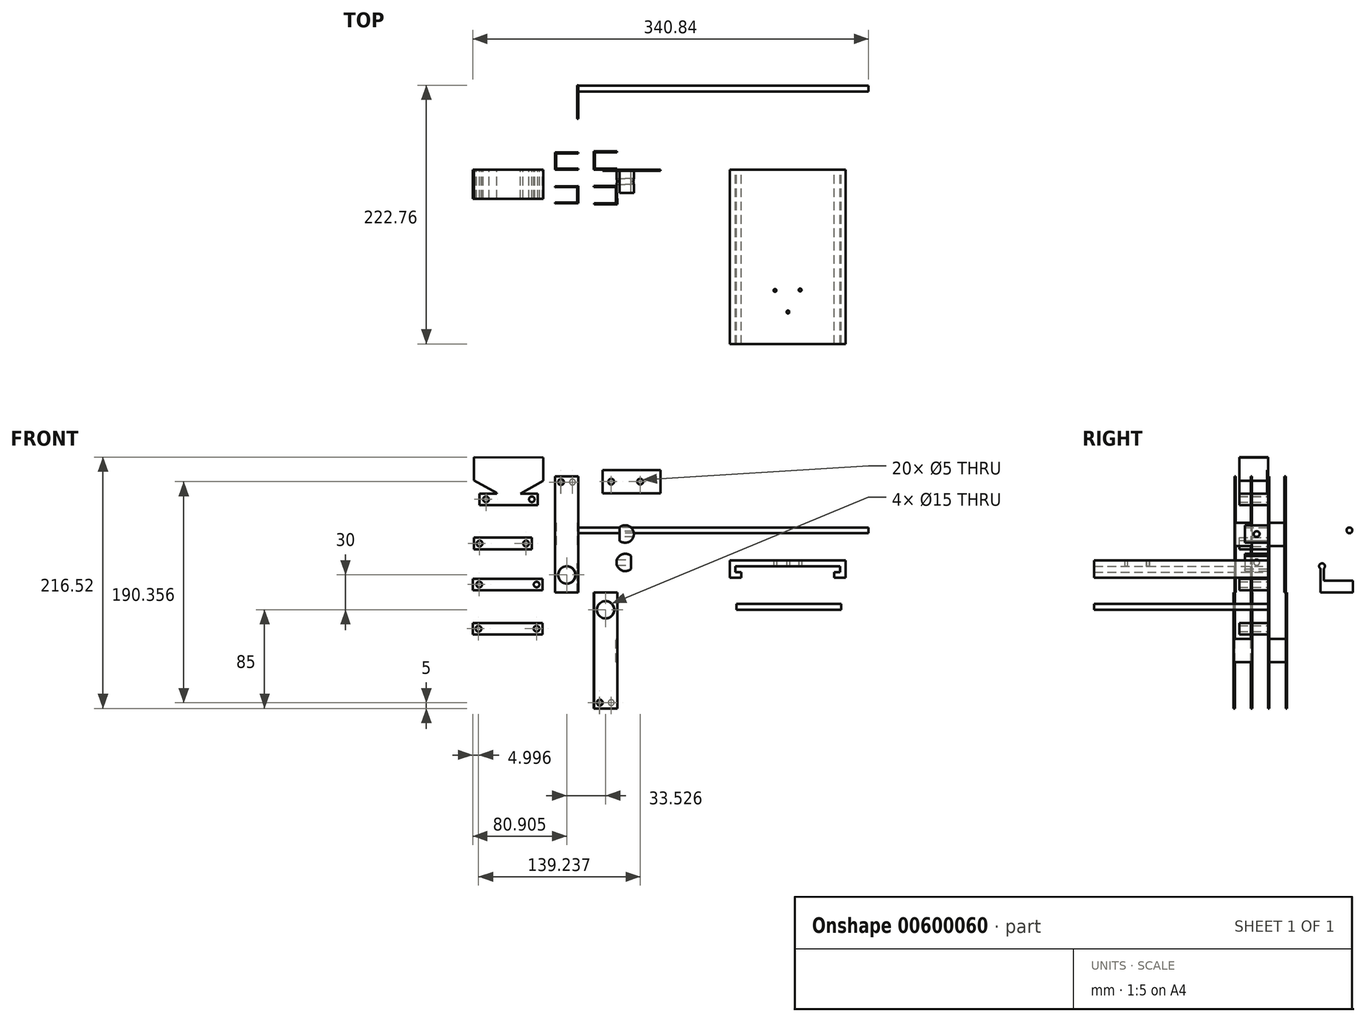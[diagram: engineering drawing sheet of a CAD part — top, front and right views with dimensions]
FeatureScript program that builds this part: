
annotation { "Feature Type Name" : "Feature", "Feature Type Description" : "" }
export const myFeature = defineFeature(function(context is Context, id is Id, definition is map)
    precondition{}
    {
        {
            var Q0;
            Q0=qCreatedBy(makeId("Top.planeOp"),FACE);
            var sketch = newSketch(context, id + "F0", { "sketchPlane" : qUnion([Q0])});
            skLineSegment(sketch, "E0", {"start": v(0, 15) * mm, "end": v(-20, 15) * mm});
            skLineSegment(sketch, "E1", {"start": v(-20, 15) * mm, "end": v(-20, 0) * mm});
            skLineSegment(sketch, "E2", {"start": v(-20, 0) * mm, "end": v(0, 0) * mm});
            skLineSegment(sketch, "E3", {"start": v(0, 0) * mm, "end": v(0, 1) * mm});
            skLineSegment(sketch, "E4", {"start": v(0, 1) * mm, "end": v(-19, 1) * mm});
            skLineSegment(sketch, "E5", {"start": v(-19, 1) * mm, "end": v(-19, 14) * mm});
            skLineSegment(sketch, "E6", {"start": v(-19, 14) * mm, "end": v(0, 14) * mm});
            skLineSegment(sketch, "E7", {"start": v(0, 14) * mm, "end": v(0, 15) * mm});
            skLineSegment(sketch, "E8", {"start": v(33.42, 1) * mm, "end": v(14.42, 1) * mm});
            skLineSegment(sketch, "E9", {"start": v(14.42, 1) * mm, "end": v(14.42, 15) * mm});
            skLineSegment(sketch, "E10", {"start": v(14.42, 15) * mm, "end": v(33.42, 15) * mm});
            skLineSegment(sketch, "E11", {"start": v(33.42, 15) * mm, "end": v(33.42, 16) * mm});
            skLineSegment(sketch, "E12", {"start": v(33.42, 16) * mm, "end": v(13.42, 16) * mm});
            skLineSegment(sketch, "E13", {"start": v(13.42, 16) * mm, "end": v(13.42, 0) * mm});
            skLineSegment(sketch, "E14", {"start": v(13.42, 0) * mm, "end": v(33.42, 0) * mm});
            skLineSegment(sketch, "E15", {"start": v(33.42, 0) * mm, "end": v(33.42, 1) * mm});
            skLineSegment(sketch, "E16", {"start": v(-36.62, -7.13) * mm, "end": v(38.64, -6.85) * mm, "construction": true});
            skLineSegment(sketch, "E17.MirrorCS", {"start": v(-19, 16) * mm, "end": v(0, 16) * mm});
            skLineSegment(sketch, "E18.MirrorCS", {"start": v(-19.95, -14.13) * mm, "end": v(0.05, -13.99) * mm});
            skLineSegment(sketch, "E19.MirrorCS", {"start": v(0.16, -28.99) * mm, "end": v(-19.84, -29.13) * mm});
            skLineSegment(sketch, "E20.MirrorCS", {"start": v(13.47, -13.89) * mm, "end": v(33.47, -13.74) * mm});
            skLineSegment(sketch, "E21.MirrorCS", {"start": v(33.58, -29.74) * mm, "end": v(13.58, -29.89) * mm});
            skLineSegment(sketch, "E22", {"start": v(13.47, -13.89) * mm, "end": v(13.47, -14.89) * mm});
            skLineSegment(sketch, "E23", {"start": v(13.47, -14.89) * mm, "end": v(32.47, -14.75) * mm});
            skLineSegment(sketch, "E24", {"start": v(32.58, -28.75) * mm, "end": v(13.58, -28.89) * mm});
            skLineSegment(sketch, "E25", {"start": v(13.58, -28.89) * mm, "end": v(13.58, -29.89) * mm});
            skLineSegment(sketch, "E26", {"start": v(32.58, -28.75) * mm, "end": v(32.47, -14.75) * mm});
            skLineSegment(sketch, "E27", {"start": v(33.47, -13.74) * mm, "end": v(33.58, -29.74) * mm});
            skLineSegment(sketch, "E28", {"start": v(0.05, -13.99) * mm, "end": v(0.16, -28.99) * mm});
            skLineSegment(sketch, "E29", {"start": v(-19.95, -14.13) * mm, "end": v(-19.94, -15.13) * mm});
            skLineSegment(sketch, "E30", {"start": v(-19.94, -15.13) * mm, "end": v(-0.94, -15) * mm});
            skLineSegment(sketch, "E31", {"start": v(-0.94, -15) * mm, "end": v(-0.85, -28) * mm});
            skLineSegment(sketch, "E32", {"start": v(-0.85, -28) * mm, "end": v(-19.84, -28.13) * mm});
            skLineSegment(sketch, "E33", {"start": v(-19.84, -29.13) * mm, "end": v(-19.84, -28.13) * mm});
            skSolve(sketch);
        }
        {
            var Q0;
            Q0=makeQuery(id+"F0.imprint","IMPRINT",FACE,{"disambiguationData":[TD([[makeQuery(id+"F0.imprint","IMPRINT",EDGE,{"derivedFrom":sQuery(id+"F0.wireOp",EDGE,"E0")}),1.0]])]});
            var Q1;
            Q1=makeQuery(id+"F0.imprint","IMPRINT",FACE,{"disambiguationData":[TD([[makeQuery(id+"F0.imprint","IMPRINT",EDGE,{"derivedFrom":sQuery(id+"F0.wireOp",EDGE,"E19.MirrorCS")}),-1.0]])]});
            extrude(context, id + "F1", {"entities" : qUnion([Q0, Q1]), "depth" : 100 * mm, "offsetDistance" : 25 * mm});
        }
        {
            var Q0;
            Q0=makeQuery(id+"F1.opExtrude","SWEPT_FACE",FACE,{"disambiguationData":[OSD([sQuery(id+"F0.wireOp",EDGE,"E2")])]});
            var sketch = newSketch(context, id + "F2", { "sketchPlane" : qUnion([Q0])});
            skCircle(sketch, "E34", {"center": v(-10, 15) * mm, "radius": 7.5 * mm});
            skPoint(sketch, "E34.centerSnap0", {"position": v(-10, 0) * mm});
            skCircle(sketch, "E35", {"center": v(-5, 95) * mm, "radius": 2.5 * mm});
            skSolve(sketch);
        }
        {
            var Q0;
            Q0=makeQuery(id+"F2.imprint","IMPRINT",FACE,{"disambiguationData":[TD([[makeQuery(id+"F2.imprint","IMPRINT",EDGE,{"derivedFrom":sQuery(id+"F2.wireOp",EDGE,"E34")}),1.0]])]});
            var Q1;
            Q1=makeQuery(id+"F2.imprint","IMPRINT",FACE,{"disambiguationData":[TD([[makeQuery(id+"F2.imprint","IMPRINT",EDGE,{"derivedFrom":sQuery(id+"F2.wireOp",EDGE,"E35")}),1.0]])]});
            extrude(context, id + "F3", {"entities" : qUnion([Q0, Q1]), "operationType" : NewBodyOperationType.REMOVE, "endBound" : BoundingType.THROUGH_ALL, "oppositeDirection" : true, "depth" : 25 * mm, "offsetDistance" : 25 * mm});
        }
        {
            var Q0;
            Q0=makeQuery(id+"F1.opExtrude","SWEPT_FACE",FACE,{"disambiguationData":[OSD([sQuery(id+"F0.wireOp",EDGE,"E1")])]});
            var sketch = newSketch(context, id + "F4", { "sketchPlane" : qUnion([Q0])});
            skPoint(sketch, "E36.centerSnap0", {"position": v(-7.5, 0) * mm});
            skLineSegment(sketch, "E37", {"start": v(-14, 0) * mm, "end": v(-14, 40) * mm});
            skLineSegment(sketch, "E38", {"start": v(-14, 40) * mm, "end": v(-1, 40) * mm});
            skLineSegment(sketch, "E39", {"start": v(-1, 40) * mm, "end": v(-1, 0) * mm});
            skLineSegment(sketch, "E40", {"start": v(-14, 100) * mm, "end": v(-14, 60) * mm});
            skLineSegment(sketch, "E41", {"start": v(-14, 60) * mm, "end": v(-1, 60) * mm});
            skLineSegment(sketch, "E42", {"start": v(-1, 60) * mm, "end": v(-1, 100) * mm});
            skSolve(sketch);
        }
        {
            var Q0;
            {var subQ0=sQuery(id+"F4.wireOp",EDGE,"E37");Q0=makeQuery(id+"F4.imprint","IMPRINT",FACE,{"disambiguationData":[TD([[makeQuery(id+"F4.imprint","IMPRINT",EDGE,{"derivedFrom":subQ0}),-1.0]])]});}
            var Q1;
            {var subQ0=sQuery(id+"F4.wireOp",EDGE,"E40");Q1=makeQuery(id+"F4.imprint","IMPRINT",FACE,{"disambiguationData":[TD([[makeQuery(id+"F4.imprint","IMPRINT",EDGE,{"derivedFrom":subQ0}),1.0]])]});}
            extrude(context, id + "F5", {"entities" : qUnion([Q0, Q1]), "operationType" : NewBodyOperationType.REMOVE, "endBound" : BoundingType.THROUGH_ALL, "oppositeDirection" : true, "depth" : 25 * mm, "offsetDistance" : 25 * mm});
        }
        {
            var Q0;
            Q0=makeQuery(id+"F0.imprint","IMPRINT",FACE,{"disambiguationData":[TD([[makeQuery(id+"F0.imprint","IMPRINT",EDGE,{"derivedFrom":sQuery(id+"F0.wireOp",EDGE,"E8")}),1.0]])]});
            var Q1;
            Q1=makeQuery(id+"F0.imprint","IMPRINT",FACE,{"disambiguationData":[TD([[makeQuery(id+"F0.imprint","IMPRINT",EDGE,{"derivedFrom":sQuery(id+"F0.wireOp",EDGE,"E20.MirrorCS")}),-1.0]])]});
            extrude(context, id + "F6", {"entities" : qUnion([Q0, Q1]), "oppositeDirection" : true, "depth" : 100 * mm, "offsetDistance" : 25 * mm});
        }
        {
            var Q0;
            Q0=makeQuery(id+"F6.opExtrude","SWEPT_FACE",FACE,{"disambiguationData":[OSD([sQuery(id+"F0.wireOp",EDGE,"E14")])]});
            var sketch = newSketch(context, id + "F7", { "sketchPlane" : qUnion([Q0])});
            skCircle(sketch, "E43", {"center": v(23.42, -15) * mm, "radius": 7.5 * mm});
            skPoint(sketch, "E43.centerSnap0", {"position": v(23.42, 0) * mm});
            skCircle(sketch, "E44", {"center": v(28.42, -95) * mm, "radius": 2.5 * mm});
            skSolve(sketch);
        }
        {
            var Q0;
            Q0=makeQuery(id+"F7.imprint","IMPRINT",FACE,{"disambiguationData":[TD([[makeQuery(id+"F7.imprint","IMPRINT",EDGE,{"derivedFrom":sQuery(id+"F7.wireOp",EDGE,"E43")}),1.0]])]});
            var Q1;
            Q1=makeQuery(id+"F7.imprint","IMPRINT",FACE,{"disambiguationData":[TD([[makeQuery(id+"F7.imprint","IMPRINT",EDGE,{"derivedFrom":sQuery(id+"F7.wireOp",EDGE,"E44")}),1.0]])]});
            extrude(context, id + "F8", {"entities" : qUnion([Q0, Q1]), "operationType" : NewBodyOperationType.REMOVE, "endBound" : BoundingType.THROUGH_ALL, "oppositeDirection" : true, "depth" : 25 * mm, "offsetDistance" : 25 * mm});
        }
        {
            var Q0;
            Q0=makeQuery(id+"F6.opExtrude","SWEPT_FACE",FACE,{"disambiguationData":[OSD([sQuery(id+"F0.wireOp",EDGE,"E13")])]});
            var sketch = newSketch(context, id + "F9", { "sketchPlane" : qUnion([Q0])});
            skLineSegment(sketch, "E45", {"start": v(-15, 0) * mm, "end": v(-15, -40) * mm});
            skLineSegment(sketch, "E46", {"start": v(-15, -40) * mm, "end": v(-1, -40) * mm});
            skLineSegment(sketch, "E47", {"start": v(-1, -40) * mm, "end": v(-1, 0) * mm});
            skLineSegment(sketch, "E48", {"start": v(-15, -100) * mm, "end": v(-15, -60) * mm});
            skLineSegment(sketch, "E49", {"start": v(-15, -60) * mm, "end": v(-1, -60) * mm});
            skLineSegment(sketch, "E50", {"start": v(-1, -60) * mm, "end": v(-1, -100) * mm});
            skSolve(sketch);
        }
        {
            var Q0;
            {var subQ0=sQuery(id+"F9.wireOp",EDGE,"E45");Q0=makeQuery(id+"F9.imprint","IMPRINT",FACE,{"disambiguationData":[TD([[makeQuery(id+"F9.imprint","IMPRINT",EDGE,{"derivedFrom":subQ0}),1.0]])]});}
            var Q1;
            {var subQ0=sQuery(id+"F9.wireOp",EDGE,"E48");Q1=makeQuery(id+"F9.imprint","IMPRINT",FACE,{"disambiguationData":[TD([[makeQuery(id+"F9.imprint","IMPRINT",EDGE,{"derivedFrom":subQ0}),-1.0]])]});}
            extrude(context, id + "F10", {"entities" : qUnion([Q0, Q1]), "operationType" : NewBodyOperationType.REMOVE, "endBound" : BoundingType.THROUGH_ALL, "oppositeDirection" : true, "depth" : 25 * mm, "offsetDistance" : 25 * mm});
        }
        {
            var Q0;
            Q0=qCreatedBy(makeId("Front.planeOp"),FACE);
            var sketch = newSketch(context, id + "F11", { "sketchPlane" : qUnion([Q0])});
            skLineSegment(sketch, "E51.bottom", {"start": v(20.9, 105.36) * mm, "end": v(70.9, 105.36) * mm});
            skLineSegment(sketch, "E51.top", {"start": v(20.9, 85.36) * mm, "end": v(70.9, 85.36) * mm});
            skLineSegment(sketch, "E51.left", {"start": v(20.9, 105.36) * mm, "end": v(20.9, 85.36) * mm});
            skLineSegment(sketch, "E51.right", {"start": v(70.9, 105.36) * mm, "end": v(70.9, 85.36) * mm});
            skCircle(sketch, "E52", {"center": v(28.4, 95.36) * mm, "radius": 2.5 * mm});
            skPoint(sketch, "E52.centerSnap0", {"position": v(20.9, 95.36) * mm});
            skCircle(sketch, "E53.MirrorC", {"center": v(53.4, 95.36) * mm, "radius": 2.5 * mm});
            skSolve(sketch);
        }
        {
            var Q0;
            Q0=makeQuery(id+"F11.imprint","IMPRINT",FACE,{"disambiguationData":[TD([[makeQuery(id+"F11.imprint","IMPRINT",EDGE,{"derivedFrom":sQuery(id+"F11.wireOp",EDGE,"E51.bottom")}),-1.0]])]});
            extrude(context, id + "F12", {"entities" : qUnion([Q0]), "depth" : 1 * mm, "offsetDistance" : 25 * mm});
        }
        {
            var Q0;
            Q0=makeQuery(id+"F1.opExtrude","SWEPT_FACE",FACE,{"disambiguationData":[OSD([sQuery(id+"F0.wireOp",EDGE,"E19.MirrorCS")])]});
            var sketch = newSketch(context, id + "F13", { "sketchPlane" : qUnion([Q0])});
            skCircle(sketch, "E54", {"center": v(-15.05, 95) * mm, "radius": 2.5 * mm});
            skCircle(sketch, "E55", {"center": v(-10.05, 15) * mm, "radius": 7.5 * mm});
            skPoint(sketch, "E55.centerSnap0", {"position": v(-10.05, 0) * mm});
            skSolve(sketch);
        }
        {
            var Q0;
            Q0=makeQuery(id+"F13.imprint","IMPRINT",FACE,{"disambiguationData":[TD([[makeQuery(id+"F13.imprint","IMPRINT",EDGE,{"derivedFrom":sQuery(id+"F13.wireOp",EDGE,"E54")}),1.0]])]});
            var Q1;
            Q1=makeQuery(id+"F13.imprint","IMPRINT",FACE,{"disambiguationData":[TD([[makeQuery(id+"F13.imprint","IMPRINT",EDGE,{"derivedFrom":sQuery(id+"F13.wireOp",EDGE,"E55")}),1.0]])]});
            extrude(context, id + "F14", {"entities" : qUnion([Q0, Q1]), "operationType" : NewBodyOperationType.REMOVE, "endBound" : BoundingType.THROUGH_ALL, "oppositeDirection" : true, "depth" : 25 * mm, "offsetDistance" : 25 * mm});
        }
        {
            var Q0;
            Q0=makeQuery(id+"F6.opExtrude","SWEPT_FACE",FACE,{"disambiguationData":[OSD([sQuery(id+"F0.wireOp",EDGE,"E21.MirrorCS")])]});
            var sketch = newSketch(context, id + "F15", { "sketchPlane" : qUnion([Q0])});
            skCircle(sketch, "E56", {"center": v(23.36, -15) * mm, "radius": 7.5 * mm});
            skPoint(sketch, "E56.centerSnap0", {"position": v(23.36, 0) * mm});
            skCircle(sketch, "E57", {"center": v(18.36, -95) * mm, "radius": 2.5 * mm});
            skSolve(sketch);
        }
        {
            var Q0;
            Q0=qSketchRegion(id+"F15",true);
            extrude(context, id + "F16", {"entities" : qUnion([Q0]), "operationType" : NewBodyOperationType.REMOVE, "endBound" : BoundingType.THROUGH_ALL, "oppositeDirection" : true, "depth" : 25 * mm, "offsetDistance" : 25 * mm});
        }
        {
            var Q0;
            Q0=makeQuery(id+"F6.opExtrude","SWEPT_FACE",FACE,{"disambiguationData":[OSD([sQuery(id+"F0.wireOp",EDGE,"E27")])]});
            var sketch = newSketch(context, id + "F17", { "sketchPlane" : qUnion([Q0])});
            skLineSegment(sketch, "E58", {"start": v(-14.99, -40) * mm, "end": v(-28.99, -40) * mm});
            skLineSegment(sketch, "E59", {"start": v(-28.99, -40) * mm, "end": v(-28.99, 0) * mm});
            skLineSegment(sketch, "E60", {"start": v(-14.99, -40) * mm, "end": v(-14.99, 0) * mm});
            skLineSegment(sketch, "E61", {"start": v(-28.99, -100) * mm, "end": v(-28.99, -60) * mm});
            skLineSegment(sketch, "E62", {"start": v(-28.99, -60) * mm, "end": v(-14.99, -60) * mm});
            skLineSegment(sketch, "E63", {"start": v(-14.99, -60) * mm, "end": v(-14.99, -100) * mm});
            skSolve(sketch);
        }
        {
            var Q0;
            Q0=makeQuery(id+"F17.imprint","IMPRINT",FACE,{"disambiguationData":[TD([[makeQuery(id+"F17.imprint","IMPRINT",EDGE,{"derivedFrom":sQuery(id+"F17.wireOp",EDGE,"E58")}),-1.0]])]});
            var Q1;
            {var subQ0=sQuery(id+"F17.wireOp",EDGE,"E61");Q1=makeQuery(id+"F17.imprint","IMPRINT",FACE,{"disambiguationData":[TD([[makeQuery(id+"F17.imprint","IMPRINT",EDGE,{"derivedFrom":subQ0}),-1.0]])]});}
            extrude(context, id + "F18", {"entities" : qUnion([Q0, Q1]), "operationType" : NewBodyOperationType.REMOVE, "endBound" : BoundingType.THROUGH_ALL, "oppositeDirection" : true, "depth" : 25 * mm, "offsetDistance" : 25 * mm});
        }
        {
            var Q0;
            Q0=makeQuery(id+"F1.opExtrude","SWEPT_FACE",FACE,{"disambiguationData":[OSD([sQuery(id+"F0.wireOp",EDGE,"E28")])]});
            var sketch = newSketch(context, id + "F19", { "sketchPlane" : qUnion([Q0])});
            skLineSegment(sketch, "E64", {"start": v(-14.99, 0) * mm, "end": v(-14.99, 40) * mm});
            skLineSegment(sketch, "E65", {"start": v(-14.99, 40) * mm, "end": v(-27.99, 40) * mm});
            skLineSegment(sketch, "E66", {"start": v(-27.99, 40) * mm, "end": v(-27.99, 0) * mm});
            skLineSegment(sketch, "E67", {"start": v(-27.99, 100) * mm, "end": v(-27.99, 60) * mm});
            skLineSegment(sketch, "E68", {"start": v(-27.99, 60) * mm, "end": v(-14.99, 60) * mm});
            skLineSegment(sketch, "E69", {"start": v(-14.99, 60) * mm, "end": v(-14.99, 100) * mm});
            skSolve(sketch);
        }
        {
            var Q0;
            {var subQ0=sQuery(id+"F19.wireOp",EDGE,"E64");Q0=makeQuery(id+"F19.imprint","IMPRINT",FACE,{"disambiguationData":[TD([[makeQuery(id+"F19.imprint","IMPRINT",EDGE,{"derivedFrom":subQ0}),1.0]])]});}
            var Q1;
            {var subQ0=sQuery(id+"F19.wireOp",EDGE,"E67");Q1=makeQuery(id+"F19.imprint","IMPRINT",FACE,{"disambiguationData":[TD([[makeQuery(id+"F19.imprint","IMPRINT",EDGE,{"derivedFrom":subQ0}),1.0]])]});}
            extrude(context, id + "F20", {"entities" : qUnion([Q0, Q1]), "operationType" : NewBodyOperationType.REMOVE, "oppositeDirection" : true, "depth" : 25 * mm, "offsetDistance" : 25 * mm});
        }
        {
            var Q0;
            Q0=qCreatedBy(makeId("Front.planeOp"),FACE);
            var sketch = newSketch(context, id + "F21", { "sketchPlane" : qUnion([Q0])});
            skArc(sketch, "E70", {"start": v(35.49, 44.6) * mm, "mid": v(47.93, 50.24) * mm, "end": v(35.49, 55.88) * mm});
            skArc(sketch, "E71", {"start": v(45.38, 31.4) * mm, "mid": v(32.93, 25.77) * mm, "end": v(45.38, 20.13) * mm});
            skLineSegment(sketch, "E72", {"start": v(35.49, 55.88) * mm, "end": v(35.49, 44.6) * mm});
            skLineSegment(sketch, "E73.trimOffspring", {"start": v(45.38, 31.4) * mm, "end": v(45.38, 20.13) * mm});
            skPoint(sketch, "E74.orphan", {"position": v(40.43, 57.74) * mm});
            skSolve(sketch);
        }
        {
            var Q0;
            Q0=makeQuery(id+"F21.imprint","IMPRINT",FACE,{"disambiguationData":[TD([[makeQuery(id+"F21.imprint","IMPRINT",EDGE,{"derivedFrom":sQuery(id+"F21.wireOp",EDGE,"E70")}),1.0]])]});
            var Q1;
            Q1=makeQuery(id+"F21.imprint","IMPRINT",FACE,{"disambiguationData":[TD([[makeQuery(id+"F21.imprint","IMPRINT",EDGE,{"derivedFrom":sQuery(id+"F21.wireOp",EDGE,"E71")}),1.0]])]});
            extrude(context, id + "F22", {"entities" : qUnion([Q0, Q1]), "depth" : 20 * mm, "offsetDistance" : 25 * mm});
        }
        {
            var Q0;
            Q0=qCreatedBy(makeId("Right.planeOp"),FACE);
            var sketch = newSketch(context, id + "F23", { "sketchPlane" : qUnion([Q0])});
            skCircle(sketch, "E75", {"center": v(69.88, 53.43) * mm, "radius": 2.5 * mm});
            skSolve(sketch);
        }
        {
            var Q0;
            Q0=makeQuery(id+"F23.imprint","IMPRINT",FACE,{"disambiguationData":[TD([[makeQuery(id+"F23.imprint","IMPRINT",EDGE,{"derivedFrom":sQuery(id+"F23.wireOp",EDGE,"E75")}),1.0]])]});
            extrude(context, id + "F24", {"entities" : qUnion([Q0]), "depth" : 250 * mm, "offsetDistance" : 25 * mm});
        }
        {
            var Q0;
            Q0=qCreatedBy(makeId("Front.planeOp"),FACE);
            var sketch = newSketch(context, id + "F25", { "sketchPlane" : qUnion([Q0])});
            skLineSegment(sketch, "E76.top", {"start": v(-84.95, 75.12) * mm, "end": v(-34.95, 75.12) * mm});
            skLineSegment(sketch, "E76.left", {"start": v(-84.95, 85.12) * mm, "end": v(-84.95, 75.12) * mm});
            skLineSegment(sketch, "E76.right", {"start": v(-34.95, 85.12) * mm, "end": v(-34.95, 75.12) * mm});
            skCircle(sketch, "E77", {"center": v(-79.38, 80.12) * mm, "radius": 2.5 * mm});
            skPoint(sketch, "E77.centerSnap0", {"position": v(-84.95, 80.12) * mm});
            skCircle(sketch, "E78", {"center": v(-39.95, 80.12) * mm, "radius": 2.41 * mm});
            skPoint(sketch, "E78.centerSnap0", {"position": v(-34.95, 80.12) * mm});
            skLineSegment(sketch, "E79.MirrorCS", {"start": v(-89.95, 47.06) * mm, "end": v(-39.95, 47.06) * mm});
            skLineSegment(sketch, "E80.MirrorCS", {"start": v(-89.95, 37.06) * mm, "end": v(-89.95, 47.06) * mm});
            skLineSegment(sketch, "E81.MirrorCS", {"start": v(-89.95, 37.06) * mm, "end": v(-39.95, 37.06) * mm});
            skLineSegment(sketch, "E82.MirrorCS", {"start": v(-39.95, 37.06) * mm, "end": v(-39.95, 47.06) * mm});
            skCircle(sketch, "E83", {"center": v(-84.95, 42.06) * mm, "radius": 2.5 * mm});
            skPoint(sketch, "E83.centerSnap0", {"position": v(-89.95, 42.06) * mm});
            skCircle(sketch, "E84", {"center": v(-44.95, 42.06) * mm, "radius": 2.5 * mm});
            skPoint(sketch, "E84.centerSnap0", {"position": v(-39.95, 42.06) * mm});
            skLineSegment(sketch, "E85.bottom", {"start": v(-90.84, 11.74) * mm, "end": v(-30.84, 11.74) * mm});
            skLineSegment(sketch, "E85.top", {"start": v(-90.84, 1.74) * mm, "end": v(-30.84, 1.74) * mm});
            skLineSegment(sketch, "E85.left", {"start": v(-90.84, 11.74) * mm, "end": v(-90.84, 1.74) * mm});
            skLineSegment(sketch, "E85.right", {"start": v(-30.84, 11.74) * mm, "end": v(-30.84, 1.74) * mm});
            skCircle(sketch, "E86", {"center": v(-85.27, 6.74) * mm, "radius": 2.5 * mm});
            skPoint(sketch, "E86.centerSnap0", {"position": v(-90.84, 6.74) * mm});
            skCircle(sketch, "E87", {"center": v(-35.84, 6.74) * mm, "radius": 2.41 * mm});
            skPoint(sketch, "E87.centerSnap0", {"position": v(-30.84, 6.74) * mm});
            skLineSegment(sketch, "E88.MirrorCS", {"start": v(-90.84, -36.32) * mm, "end": v(-90.84, -26.32) * mm});
            skLineSegment(sketch, "E89.MirrorCS", {"start": v(-30.84, -36.32) * mm, "end": v(-30.84, -26.32) * mm});
            skCircle(sketch, "E90", {"center": v(-85.84, -31.32) * mm, "radius": 2.5 * mm});
            skPoint(sketch, "E90.centerSnap0", {"position": v(-90.84, -31.32) * mm});
            skCircle(sketch, "E91", {"center": v(-35.84, -31.32) * mm, "radius": 2.5 * mm});
            skPoint(sketch, "E91.centerSnap0", {"position": v(-30.84, -31.32) * mm});
            skLineSegment(sketch, "E92", {"start": v(-90.84, -26.32) * mm, "end": v(-30.84, -26.32) * mm});
            skLineSegment(sketch, "E93", {"start": v(-90.84, -36.32) * mm, "end": v(-30.84, -36.32) * mm});
            skLineSegment(sketch, "E94", {"start": v(-69.95, 85.12) * mm, "end": v(-69.95, 85.56) * mm});
            skLineSegment(sketch, "E95.MirrorCS", {"start": v(-49.95, 85.12) * mm, "end": v(-49.95, 85.12) * mm});
            skLineSegment(sketch, "E96.MirrorCS", {"start": v(-89.95, 135.12) * mm, "end": v(-39.95, 135.12) * mm});
            skLineSegment(sketch, "E97.MirrorCS", {"start": v(-84.95, 85.12) * mm, "end": v(-69.95, 85.12) * mm});
            skLineSegment(sketch, "E98", {"start": v(-89.95, 96.52) * mm, "end": v(-89.95, 116.52) * mm});
            skLineSegment(sketch, "E99", {"start": v(-29.95, 116.08) * mm, "end": v(-29.95, 96.08) * mm});
            skLineSegment(sketch, "E100.trimOffspring", {"start": v(-49.95, 85.12) * mm, "end": v(-29.95, 96.08) * mm});
            skLineSegment(sketch, "E101", {"start": v(-69.95, 85.56) * mm, "end": v(-89.95, 96.52) * mm});
            skLineSegment(sketch, "E102.trimOffspring", {"start": v(-49.95, 85.12) * mm, "end": v(-34.95, 85.12) * mm});
            skPoint(sketch, "E103.end.orphan", {"position": v(-59.95, 75.12) * mm});
            skPoint(sketch, "E103.start.orphan", {"position": v(-59.95, 85.12) * mm});
            skLineSegment(sketch, "E104", {"start": v(-29.95, 116.08) * mm, "end": v(-89.95, 116.52) * mm});
            skLineSegment(sketch, "E105", {"start": v(-59.95, 75.12) * mm, "end": v(-59.95, 116.3) * mm, "construction": true});
            skSolve(sketch);
        }
        {
            var Q0;
            Q0=makeQuery(id+"F25.imprint","IMPRINT",FACE,{"disambiguationData":[TD([[makeQuery(id+"F25.imprint","IMPRINT",EDGE,{"derivedFrom":sQuery(id+"F25.wireOp",EDGE,"E76.bottom")}),-1.0]])]});
            var Q1;
            {var subQ2=sQuery(id+"F25.wireOp",EDGE,"E80.MirrorCS");Q1=makeQuery(id+"F25.imprint","IMPRINT",FACE,{"disambiguationData":[TD([[makeQuery(id+"F25.imprint","IMPRINT",EDGE,{"derivedFrom":subQ2}),-1.0]])]});}
            var Q2;
            Q2=makeQuery(id+"F25.imprint","IMPRINT",FACE,{"disambiguationData":[TD([[makeQuery(id+"F25.imprint","IMPRINT",EDGE,{"derivedFrom":sQuery(id+"F25.wireOp",EDGE,"E76.top")}),1.0]])]});
            extrude(context, id + "F26", {"entities" : qUnion([Q0, Q1, Q2]), "depth" : 25 * mm, "offsetDistance" : 25 * mm});
        }
        {
            var Q0;
            Q0=makeQuery(id+"F25.imprint","IMPRINT",FACE,{"disambiguationData":[TD([[makeQuery(id+"F25.imprint","IMPRINT",EDGE,{"derivedFrom":sQuery(id+"F25.wireOp",EDGE,"E88.MirrorCS")}),-1.0]])]});
            var Q1;
            Q1=makeQuery(id+"F25.imprint","IMPRINT",FACE,{"disambiguationData":[TD([[makeQuery(id+"F25.imprint","IMPRINT",EDGE,{"derivedFrom":sQuery(id+"F25.wireOp",EDGE,"E85.bottom")}),-1.0]])]});
            extrude(context, id + "F27", {"entities" : qUnion([Q0, Q1]), "depth" : 25 * mm, "offsetDistance" : 25 * mm});
        }
        {
            var Q0;
            Q0=makeQuery(id+"F22.opExtrude","SWEPT_FACE",FACE,{"disambiguationData":[OSD([sQuery(id+"F21.wireOp",EDGE,"E73.trimOffspring")])]});
            var sketch = newSketch(context, id + "F28", { "sketchPlane" : qUnion([Q0])});
            skCircle(sketch, "E106", {"center": v(-10, 25.77) * mm, "radius": 2.5 * mm});
            skPoint(sketch, "E106.centerSnap0", {"position": v(-20, 25.77) * mm});
            skPoint(sketch, "E106.centerSnap1", {"position": v(-10, 31.4) * mm});
            skSolve(sketch);
        }
        {
            var Q0;
            Q0=makeQuery(id+"F28.imprint","IMPRINT",FACE,{"disambiguationData":[TD([[makeQuery(id+"F28.imprint","IMPRINT",EDGE,{"derivedFrom":sQuery(id+"F28.wireOp",EDGE,"E106")}),1.0]])]});
            extrude(context, id + "F29", {"entities" : qUnion([Q0]), "operationType" : NewBodyOperationType.REMOVE, "endBound" : BoundingType.THROUGH_ALL, "oppositeDirection" : true, "depth" : 25 * mm, "offsetDistance" : 25 * mm});
        }
        {
            var Q0;
            Q0=makeQuery(id+"F22.opExtrude","SWEPT_FACE",FACE,{"disambiguationData":[OSD([sQuery(id+"F21.wireOp",EDGE,"E72")])]});
            var sketch = newSketch(context, id + "F30", { "sketchPlane" : qUnion([Q0])});
            skCircle(sketch, "E107", {"center": v(10, 50.24) * mm, "radius": 2.5 * mm});
            skPoint(sketch, "E107.centerSnap0", {"position": v(10, 44.6) * mm});
            skPoint(sketch, "E107.centerSnap1", {"position": v(0, 50.24) * mm});
            skSolve(sketch);
        }
        {
            var Q0;
            Q0=makeQuery(id+"F30.imprint","IMPRINT",FACE,{"disambiguationData":[TD([[makeQuery(id+"F30.imprint","IMPRINT",EDGE,{"derivedFrom":sQuery(id+"F30.wireOp",EDGE,"E107")}),1.0]])]});
            extrude(context, id + "F31", {"entities" : qUnion([Q0]), "operationType" : NewBodyOperationType.REMOVE, "endBound" : BoundingType.THROUGH_ALL, "oppositeDirection" : true, "depth" : 25 * mm, "offsetDistance" : 25 * mm});
        }
        {
            var Q0;
            Q0=qCreatedBy(makeId("Right.planeOp"),FACE);
            var sketch = newSketch(context, id + "F32", { "sketchPlane" : qUnion([Q0])});
            skArc(sketch, "E108", {"start": v(47.76, 20.47) * mm, "mid": v(46.3, 25) * mm, "end": v(44.85, 20.47) * mm});
            skLineSegment(sketch, "E109", {"start": v(47.76, 8.68) * mm, "end": v(47.76, 20.47) * mm});
            skLineSegment(sketch, "E110.MirrorCS", {"start": v(44.85, 8.68) * mm, "end": v(44.85, 20.47) * mm});
            skLineSegment(sketch, "E111", {"start": v(37.92, 27.31) * mm, "end": v(57.96, 27.31) * mm, "construction": true});
            skLineSegment(sketch, "E112", {"start": v(44.85, 8.68) * mm, "end": v(44.85, 0) * mm});
            skLineSegment(sketch, "E113", {"start": v(44.85, 0) * mm, "end": v(47.76, 0) * mm});
            skLineSegment(sketch, "E114", {"start": v(47.76, 0) * mm, "end": v(47.76, 8.68) * mm});
            skArc(sketch, "E115.MirrorCS", {"start": v(47.76, 34.16) * mm, "mid": v(46.3, 29.63) * mm, "end": v(44.85, 34.16) * mm});
            skLineSegment(sketch, "E116.MirrorCS", {"start": v(44.85, 45.94) * mm, "end": v(44.85, 34.16) * mm});
            skLineSegment(sketch, "E117.MirrorCS", {"start": v(47.76, 45.94) * mm, "end": v(47.76, 34.16) * mm});
            skLineSegment(sketch, "E118.MirrorCS", {"start": v(44.85, 45.94) * mm, "end": v(44.85, 54.62) * mm});
            skLineSegment(sketch, "E119.MirrorCS", {"start": v(47.76, 54.62) * mm, "end": v(47.76, 45.94) * mm});
            skLineSegment(sketch, "E120.MirrorCS", {"start": v(44.85, 54.62) * mm, "end": v(47.76, 54.62) * mm});
            skSolve(sketch);
        }
        {
            var Q0;
            Q0=makeQuery(id+"F32.imprint","IMPRINT",FACE,{"disambiguationData":[TD([[makeQuery(id+"F32.imprint","IMPRINT",EDGE,{"derivedFrom":sQuery(id+"F32.wireOp",EDGE,"E108")}),1.0]])]});
            var Q1;
            Q1=makeQuery(id+"F32.imprint","IMPRINT",FACE,{"disambiguationData":[TD([[makeQuery(id+"F32.imprint","IMPRINT",EDGE,{"derivedFrom":sQuery(id+"F32.wireOp",EDGE,"E115.MirrorCS")}),-1.0]])]});
            extrude(context, id + "F33", {"entities" : qUnion([Q0, Q1]), "oppositeDirection" : true, "depth" : 1 * mm, "offsetDistance" : 25 * mm});
        }
        {
            var Q0;
            Q0=makeQuery(id+"F33.opExtrude","SWEPT_FACE",FACE,{"disambiguationData":[OSD([sQuery(id+"F32.wireOp",EDGE,"E109"),sQuery(id+"F32.wireOp",EDGE,"E114")])]});
            var sketch = newSketch(context, id + "F34", { "sketchPlane" : qUnion([Q0])});
            skLineSegment(sketch, "E121", {"start": v(0, 10) * mm, "end": v(1, 10) * mm});
            skLineSegment(sketch, "E122", {"start": v(0.98, 44.62) * mm, "end": v(0, 44.62) * mm});
            skSolve(sketch);
        }
        {
            var Q0;
            {var subQ0=sQuery(id+"F34.wireOp",EDGE,"E121");Q0=makeQuery(id+"F34.imprint","IMPRINT",FACE,{"disambiguationData":[TD([[makeQuery(id+"F34.imprint","IMPRINT",EDGE,{"derivedFrom":subQ0}),-1.0]])]});}
            extrude(context, id + "F35", {"entities" : qUnion([Q0]), "operationType" : NewBodyOperationType.ADD, "depth" : 25 * mm, "offsetDistance" : 25 * mm});
        }
        {
            var Q0;
            Q0=qCreatedBy(makeId("Front.planeOp"),FACE);
            var sketch = newSketch(context, id + "F36", { "sketchPlane" : qUnion([Q0])});
            skLineSegment(sketch, "E123", {"start": v(181.33, -15) * mm, "end": v(136.33, -15) * mm});
            skLineSegment(sketch, "E124", {"start": v(136.33, -15) * mm, "end": v(136.33, -10) * mm});
            skLineSegment(sketch, "E125", {"start": v(136.33, -10) * mm, "end": v(181.33, -10) * mm});
            skLineSegment(sketch, "E126", {"start": v(181.33, -10) * mm, "end": v(181.33, -15) * mm, "construction": true});
            skLineSegment(sketch, "E127.MirrorCS", {"start": v(226.33, -10) * mm, "end": v(181.33, -10) * mm});
            skLineSegment(sketch, "E128.MirrorCS", {"start": v(181.33, -15) * mm, "end": v(226.33, -15) * mm});
            skLineSegment(sketch, "E129.MirrorCS", {"start": v(226.33, -15) * mm, "end": v(226.33, -10) * mm});
            skLineSegment(sketch, "E130", {"start": v(119.38, 8.74) * mm, "end": v(249.77, 8.74) * mm, "construction": true});
            skLineSegment(sketch, "E131.MirrorCS", {"start": v(243.3, 8.74) * mm, "end": v(112.9, 8.74) * mm, "construction": true});
            skLineSegment(sketch, "E132.MirrorCS", {"start": v(180.38, 22.49) * mm, "end": v(180.38, 27.49) * mm, "construction": true});
            skLineSegment(sketch, "E133.MirrorCS", {"start": v(220.38, 12.49) * mm, "end": v(220.38, 17.49) * mm});
            skLineSegment(sketch, "E134.MirrorCS", {"start": v(135.38, 17.49) * mm, "end": v(140.38, 17.49) * mm});
            skLineSegment(sketch, "E135.MirrorCS", {"start": v(140.38, 12.49) * mm, "end": v(140.38, 17.49) * mm});
            skLineSegment(sketch, "E136.MirrorCS", {"start": v(135.38, 22.49) * mm, "end": v(135.38, 17.49) * mm});
            skLineSegment(sketch, "E137.MirrorCS", {"start": v(225.38, 17.49) * mm, "end": v(220.38, 17.49) * mm});
            skLineSegment(sketch, "E138.MirrorCS", {"start": v(225.38, 22.49) * mm, "end": v(225.38, 17.49) * mm});
            skLineSegment(sketch, "E139.MirrorCS", {"start": v(140.38, 12.49) * mm, "end": v(130.38, 12.49) * mm});
            skLineSegment(sketch, "E140.MirrorCS", {"start": v(220.38, 12.49) * mm, "end": v(230.38, 12.49) * mm});
            skLineSegment(sketch, "E141.MirrorCS", {"start": v(230.38, 27.49) * mm, "end": v(230.38, 12.49) * mm});
            skLineSegment(sketch, "E142.MirrorCS", {"start": v(230.38, 27.49) * mm, "end": v(180.38, 27.49) * mm});
            skLineSegment(sketch, "E143.MirrorCS", {"start": v(135.38, 22.49) * mm, "end": v(180.38, 22.49) * mm});
            skLineSegment(sketch, "E144.MirrorCS", {"start": v(225.38, 22.49) * mm, "end": v(180.38, 22.49) * mm});
            skLineSegment(sketch, "E145.MirrorCS", {"start": v(130.38, 27.49) * mm, "end": v(180.38, 27.49) * mm});
            skLineSegment(sketch, "E146.MirrorCS", {"start": v(130.38, 27.49) * mm, "end": v(130.38, 12.49) * mm});
            skSolve(sketch);
        }
        {
            var Q0;
            Q0=makeQuery(id+"F36.imprint","IMPRINT",FACE,{"disambiguationData":[TD([[makeQuery(id+"F36.imprint","IMPRINT",EDGE,{"derivedFrom":sQuery(id+"F36.wireOp",EDGE,"E135.MirrorCS")}),1.0]])]});
            var Q1;
            Q1=makeQuery(id+"F36.imprint","IMPRINT",FACE,{"disambiguationData":[TD([[makeQuery(id+"F36.imprint","IMPRINT",EDGE,{"derivedFrom":sQuery(id+"F36.wireOp",EDGE,"E124")}),-1.0]])]});
            extrude(context, id + "F37", {"entities" : qUnion([Q0, Q1]), "depth" : 150 * mm, "offsetDistance" : 25 * mm});
        }
        {
            var Q0;
            Q0=makeQuery(id+"F37.opExtrude","SWEPT_FACE",FACE,{"disambiguationData":[OSD([sQuery(id+"F36.wireOp",EDGE,"E143.MirrorCS"),sQuery(id+"F36.wireOp",EDGE,"E144.MirrorCS")])]});
            var sketch = newSketch(context, id + "F38", { "sketchPlane" : qUnion([Q0])});
            skLineSegment(sketch, "E147", {"start": v(135.38, 70) * mm, "end": v(225.38, 70) * mm});
            skCircle(sketch, "E148", {"center": v(180.38, 110) * mm, "radius": 12.5 * mm, "construction": true});
            skPoint(sketch, "E148.centerSnap0", {"position": v(180.38, 150) * mm});
            skCircle(sketch, "E149", {"center": v(180.59, 122.5) * mm, "radius": 1.25 * mm});
            skCircle(sketch, "E150", {"center": v(169.45, 103.93) * mm, "radius": 1.25 * mm});
            skCircle(sketch, "E151", {"center": v(191.1, 103.57) * mm, "radius": 1.25 * mm});
            skLineSegment(sketch, "E152", {"start": v(180.59, 122.5) * mm, "end": v(169.45, 103.93) * mm, "construction": true});
            skLineSegment(sketch, "E153", {"start": v(191.1, 103.57) * mm, "end": v(180.59, 122.5) * mm, "construction": true});
            skLineSegment(sketch, "E154", {"start": v(191.1, 103.57) * mm, "end": v(169.45, 103.93) * mm, "construction": true});
            skSolve(sketch);
        }
        {
            var Q0;
            Q0=makeQuery(id+"F38.imprint","IMPRINT",FACE,{"disambiguationData":[TD([[makeQuery(id+"F38.imprint","IMPRINT",EDGE,{"derivedFrom":sQuery(id+"F38.wireOp",EDGE,"E149")}),1.0]])]});
            var Q1;
            Q1=makeQuery(id+"F38.imprint","IMPRINT",FACE,{"disambiguationData":[TD([[makeQuery(id+"F38.imprint","IMPRINT",EDGE,{"derivedFrom":sQuery(id+"F38.wireOp",EDGE,"E150")}),1.0]])]});
            var Q2;
            Q2=makeQuery(id+"F38.imprint","IMPRINT",FACE,{"disambiguationData":[TD([[makeQuery(id+"F38.imprint","IMPRINT",EDGE,{"derivedFrom":sQuery(id+"F38.wireOp",EDGE,"E151")}),1.0]])]});
            extrude(context, id + "F39", {"entities" : qUnion([Q0, Q1, Q2]), "operationType" : NewBodyOperationType.REMOVE, "endBound" : BoundingType.THROUGH_ALL, "oppositeDirection" : true, "depth" : 1 * mm, "offsetDistance" : 25 * mm});
        }
    });
